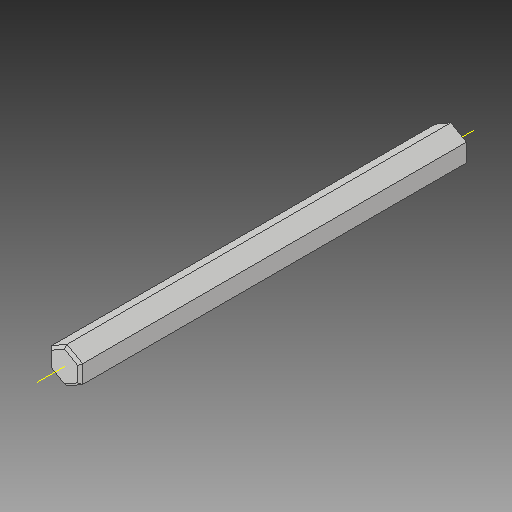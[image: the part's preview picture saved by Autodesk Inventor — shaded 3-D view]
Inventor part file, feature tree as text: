
AUTODESK INVENTOR PART (.ipt)
format: ipt  version: 2017 (Build 210142000, 142)  size: 101,888 bytes
history: native  units: in
note: dims shown in document units (in); Inventor stores cm internally (conversion verified against a paired STEP export)
features: other x4, sketch x2
ambient origin geometry x8: Origin, YZ Plane, XZ Plane, XY Plane, X Axis, Y Axis, Z Axis, Center Point
bodies: Solid1 (feature_tree)
feature tree (6):
  other  "REV-41-1349HexAxle.ipt"
  other  "Solid2::REV-41-1349HexAxle.ipt"
  other  "TaggingFeature1"
  sketch  "Sketch1"  dims[d0=0.3937in]
  sketch  "Sketch2"
  other  "Work Axis1"
